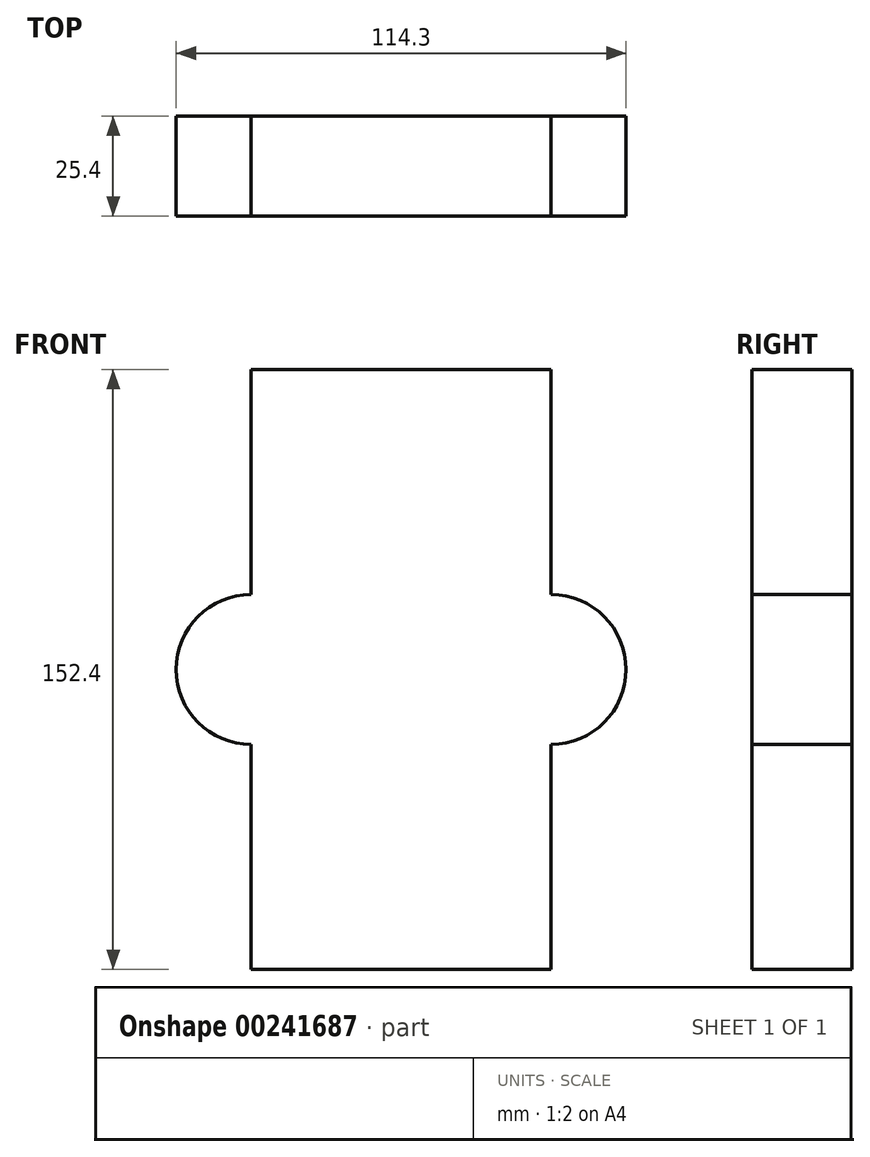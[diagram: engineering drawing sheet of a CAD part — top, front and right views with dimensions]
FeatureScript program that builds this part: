
annotation { "Feature Type Name" : "Feature", "Feature Type Description" : "" }
export const myFeature = defineFeature(function(context is Context, id is Id, definition is map)
    precondition{}
    {
        {
            var Q0;
            Q0=qCreatedBy(makeId("Front.planeOp"),FACE);
            var sketch = newSketch(context, id + "F0", { "sketchPlane" : qUnion([Q0])});
            skLineSegment(sketch, "E0.bottom", {"start": v(38.1, 76.2) * mm, "end": v(-38.1, 76.2) * mm});
            skLineSegment(sketch, "E0.top", {"start": v(38.1, -76.2) * mm, "end": v(-38.1, -76.2) * mm});
            skLineSegment(sketch, "E0.left", {"start": v(38.1, 76.2) * mm, "end": v(38.1, -76.2) * mm});
            skLineSegment(sketch, "E0.right", {"start": v(-38.1, 76.2) * mm, "end": v(-38.1, -76.2) * mm});
            skPoint(sketch, "E0.middle", {"position": v(0, 0) * mm});
            skCircle(sketch, "E1", {"center": v(-38.1, 0) * mm, "radius": 19.05 * mm});
            skCircle(sketch, "E2", {"center": v(38.1, 0) * mm, "radius": 19.05 * mm});
            skSolve(sketch);
        }
        {
            var Q0;
            Q0 = qSketchRegion(id + "F0", true);
            extrude(context, id + "F1", {"entities" : qUnion([Q0]), "oppositeDirection" : true, "depth" : 25.4 * mm});
        }
    });
